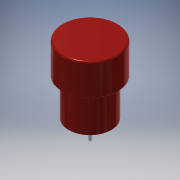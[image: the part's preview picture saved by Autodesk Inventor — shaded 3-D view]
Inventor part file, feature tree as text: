
AUTODESK INVENTOR PART (.ipt)
format: ipt  version: 2019 (Build 230136000, 136)  size: 244,224 bytes
history: native  units: mm
features: fillet x8, extrude x7, sketch x7
ambient origin geometry x8: Origin, YZ Plane, XZ Plane, XY Plane, X Axis, Y Axis, Z Axis, Center Point
bodies: Solid1 (feature_tree)
feature tree (22):
  extrude  "Extrusion1"  Depth=44.0mm TaperAngle=0.0deg
  extrude  "Extrusion2"  Depth=34.0mm TaperAngle=0.0deg
  extrude  "Extrusion3"  Depth=4.0mm TaperAngle=0.0deg
  fillet  "Fillet1"  Radius=2.0mm
  fillet  "Fillet2"  Radius=2.0mm
  fillet  "Fillet4"  Radius=2.0mm
  fillet  "Fillet5"  Radius=0.5mm
  extrude  "Extrusion7"  Depth=3.0mm
  extrude  "Extrusion8"  Depth=3.0mm
  extrude  "Extrusion9"  Depth=2.0mm
  extrude  "Extrusion10"  Depth=0.1mm
  fillet  "Fillet8"  Radius=0.2mm
  fillet  "Fillet9"  Radius=1.0mm
  fillet  "Fillet10"  Radius=0.1mm
  fillet  "Fillet11"  [1 undecoded]
  sketch  "Sketch1"  dims[d0=46.0mm d1=44.0mm d2=0.0mm]
  sketch  "Sketch2"  dims[d3=60.0mm d4=34.0mm d5=0.0mm]
  sketch  "Sketch3"  dims[d6=2.0mm d7=4.0mm d8=0.0mm d9=2.0mm d10=2.0mm d12=2.0mm d13=0.5mm]
  sketch  "Sketch8"  dims[d25=3.0mm d26=0.0mm d27=6.0mm]
  sketch  "Sketch9"  dims[d28=10.0mm d29=0.0mm d30=3.0mm]
  sketch  "Sketch10"  dims[d31=30.0mm d32=0.0mm d33=2.0mm]
  sketch  "Sketch11"  dims[d34=10.0mm d35=0.0mm d36=5.0mm d37=0.2mm d38=1.0mm d39=0.1mm]
note: 1 required parameter value undecoded (feature->parameter linkage not recoverable at this tier; creation-order binding heuristic only, values carry confidence <= 0.55)
